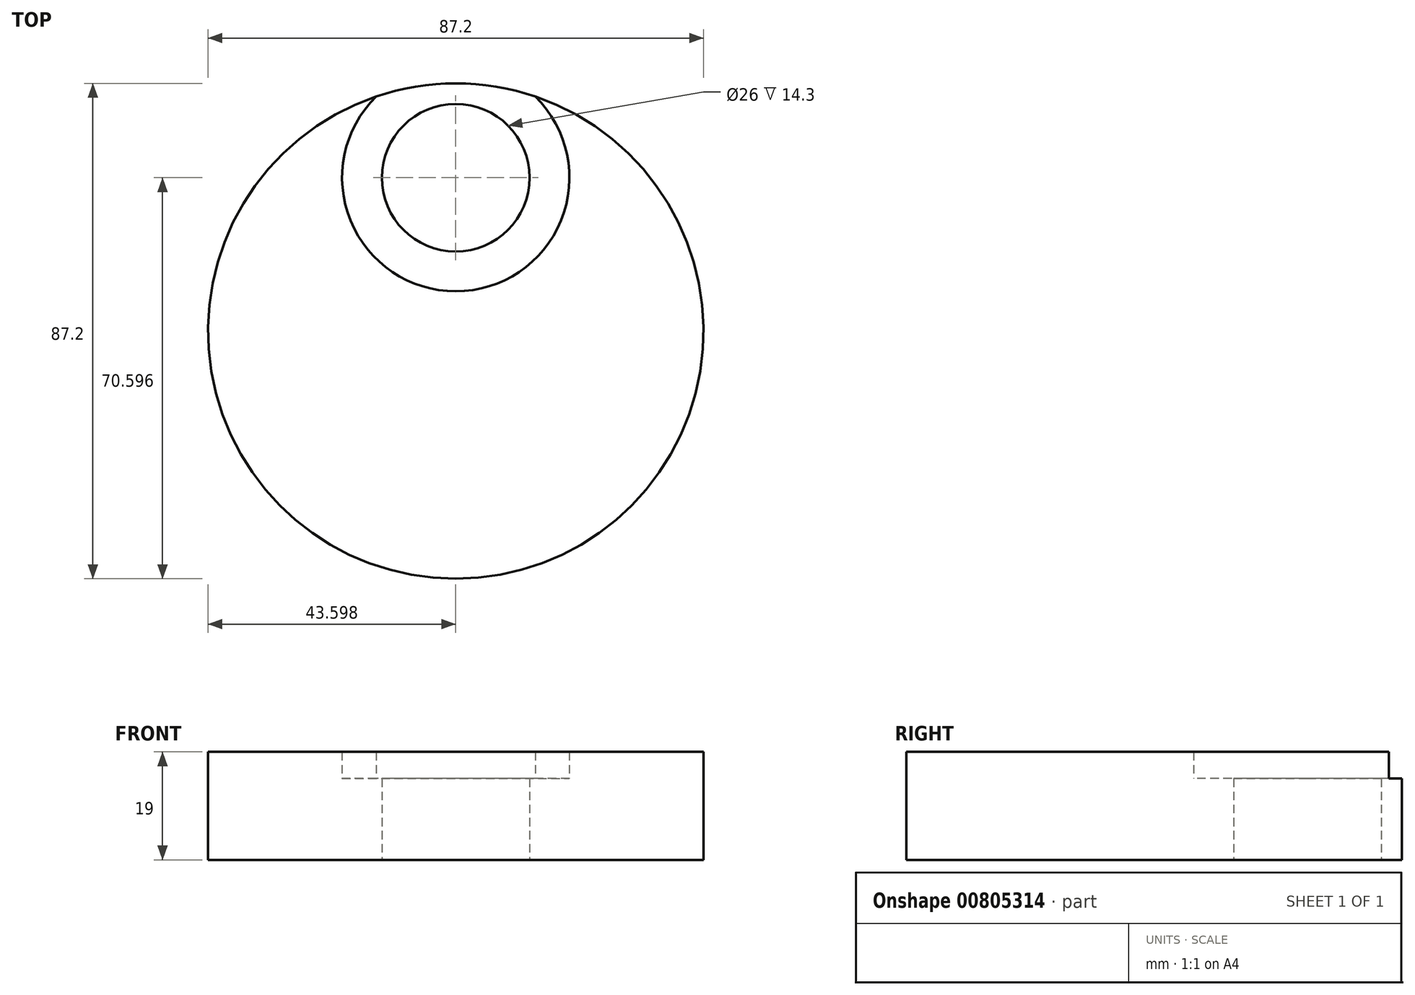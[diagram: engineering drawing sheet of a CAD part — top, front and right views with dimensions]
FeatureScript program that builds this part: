
annotation { "Feature Type Name" : "Feature", "Feature Type Description" : "" }
export const myFeature = defineFeature(function(context is Context, id is Id, definition is map)
    precondition{}
    {
        {
            var Q0;
            Q0=qCreatedBy(makeId("Top.planeOp"),FACE);
            var sketch = newSketch(context, id + "F0", { "sketchPlane" : qUnion([Q0])});
            skCircle(sketch, "E0", {"center": v(-29.76, -0.17) * mm, "radius": 43.6 * mm});
            skCircle(sketch, "E1", {"center": v(-29.76, 26.83) * mm, "radius": 13 * mm});
            skArc(sketch, "E2", {"start": v(-43.75, 41.12) * mm, "mid": v(-29.76, 6.83) * mm, "end": v(-15.78, 41.12) * mm});
            skSolve(sketch);
        }
        {
            var Q0;
            {var subQ0=sQuery(id+"F0.wireOp",EDGE,"E2");Q0=makeQuery(id+"F0.imprint","IMPRINT",FACE,{"disambiguationData":[TD([[makeQuery(id+"F0.imprint","IMPRINT",EDGE,{"derivedFrom":subQ0}),-1.0]])]});}
            extrude(context, id + "F1", {"entities" : qUnion([Q0]), "depth" : 19 * mm, "offsetDistance" : 25 * mm});
        }
        {
            var Q0;
            Q0=makeQuery(id+"F0.imprint","IMPRINT",FACE,{"disambiguationData":[TD([[makeQuery(id+"F0.imprint","IMPRINT",EDGE,{"derivedFrom":sQuery(id+"F0.wireOp",EDGE,"E1")}),-1.0]])]});
            extrude(context, id + "F2", {"entities" : qUnion([Q0]), "operationType" : NewBodyOperationType.ADD, "depth" : 14.3 * mm, "offsetDistance" : 25 * mm});
        }
    });
